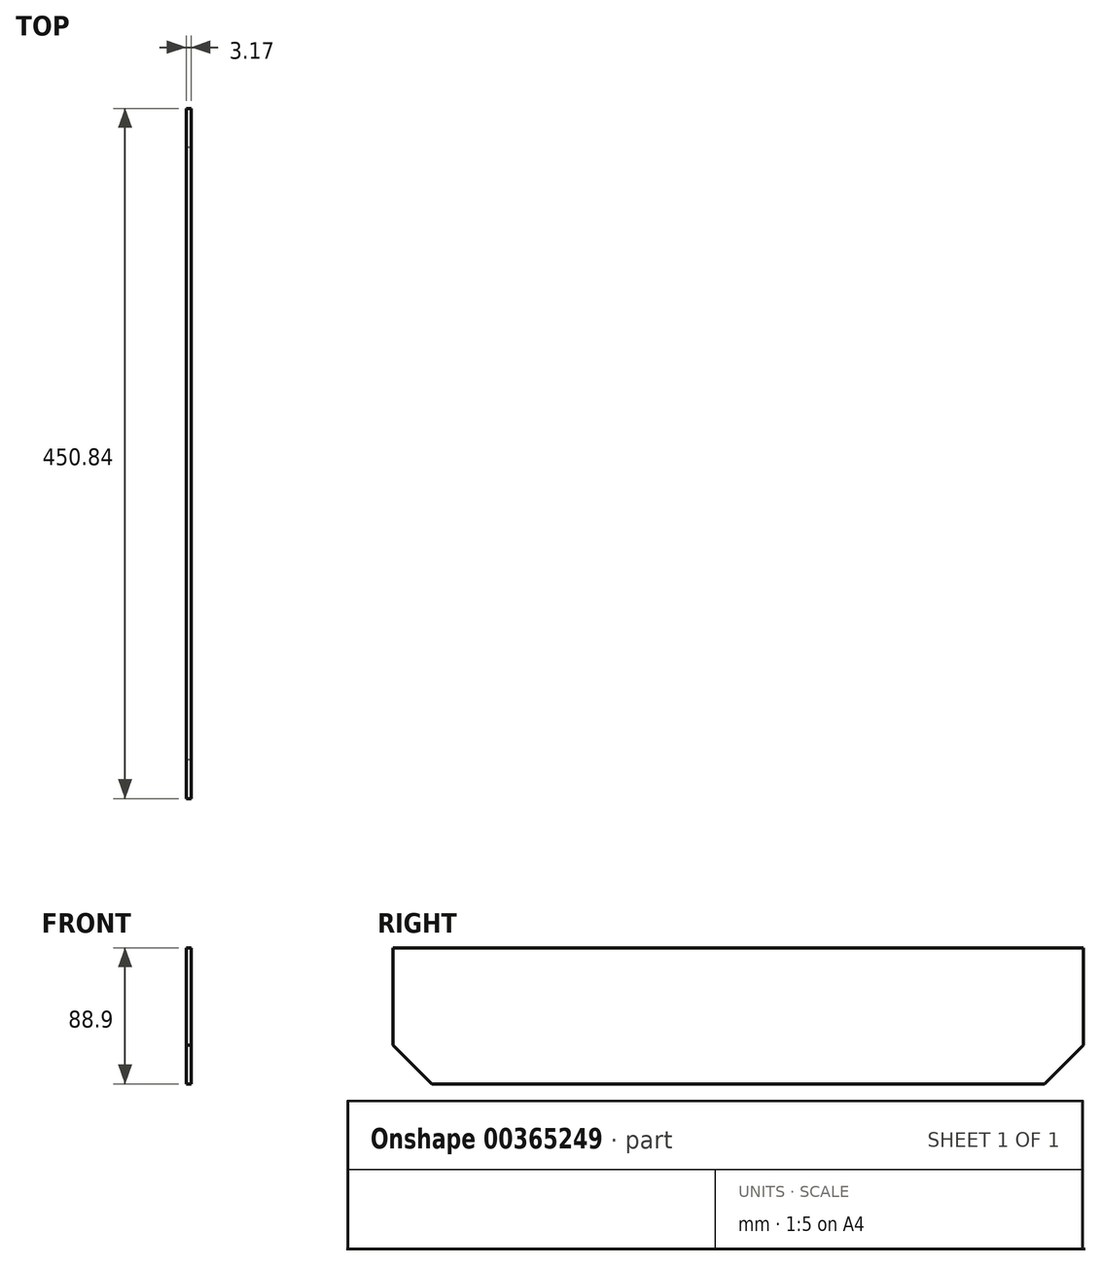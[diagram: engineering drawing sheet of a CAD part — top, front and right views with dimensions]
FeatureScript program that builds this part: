
annotation { "Feature Type Name" : "Feature", "Feature Type Description" : "" }
export const myFeature = defineFeature(function(context is Context, id is Id, definition is map)
    precondition{}
    {
        {
            var Q0;
            Q0=qCreatedBy(makeId("Right.planeOp"),FACE);
            cPlane(context, id + "F0", {"entities" : qUnion([Q0]), "cplaneType" : CPlaneType.OFFSET, "offset" : 142.88 * mm, "width" : 152.4 * mm, "height" : 152.4 * mm});
        }
        {
            var Q0;
            Q0=qCreatedBy(id+"F0.planeOp",FACE);
            var sketch = newSketch(context, id + "F1", { "sketchPlane" : qUnion([Q0])});
            skLineSegment(sketch, "E0.bottom", {"start": v(225.42, 44.45) * mm, "end": v(-225.43, 44.45) * mm});
            skLineSegment(sketch, "E0.top", {"start": v(200.02, -44.45) * mm, "end": v(-200.02, -44.45) * mm});
            skLineSegment(sketch, "E0.left", {"start": v(225.42, 44.45) * mm, "end": v(225.42, -19.05) * mm});
            skLineSegment(sketch, "E0.right", {"start": v(-225.43, 44.45) * mm, "end": v(-225.43, -19.05) * mm});
            skPoint(sketch, "E0.middle", {"position": v(0, 0) * mm});
            skLineSegment(sketch, "E1", {"start": v(-225.42, -19.05) * mm, "end": v(-200.02, -44.45) * mm});
            skLineSegment(sketch, "E2.MirrorCS", {"start": v(225.42, -19.05) * mm, "end": v(200.02, -44.45) * mm});
            skPoint(sketch, "E3.orphan", {"position": v(-225.42, -44.45) * mm});
            skLineSegment(sketch, "E4", {"start": v(-225.42, -19.05) * mm, "end": v(-225.42, -44.45) * mm, "construction": true});
            skLineSegment(sketch, "E5", {"start": v(-200.02, -44.45) * mm, "end": v(-225.42, -44.45) * mm, "construction": true});
            skPoint(sketch, "E6.orphan", {"position": v(225.43, -44.45) * mm});
            skSolve(sketch);
        }
        {
            var Q0;
            Q0=makeQuery(id+"F1.imprint","IMPRINT",FACE,{"disambiguationData":[TD([[makeQuery(id+"F1.imprint","IMPRINT",EDGE,{"derivedFrom":sQuery(id+"F1.wireOp",EDGE,"E0.bottom")}),1.0]])]});
            extrude(context, id + "F2", {"entities" : qUnion([Q0]), "depth" : 3.17 * mm, "offsetDistance" : 25.4 * mm});
        }
    });
